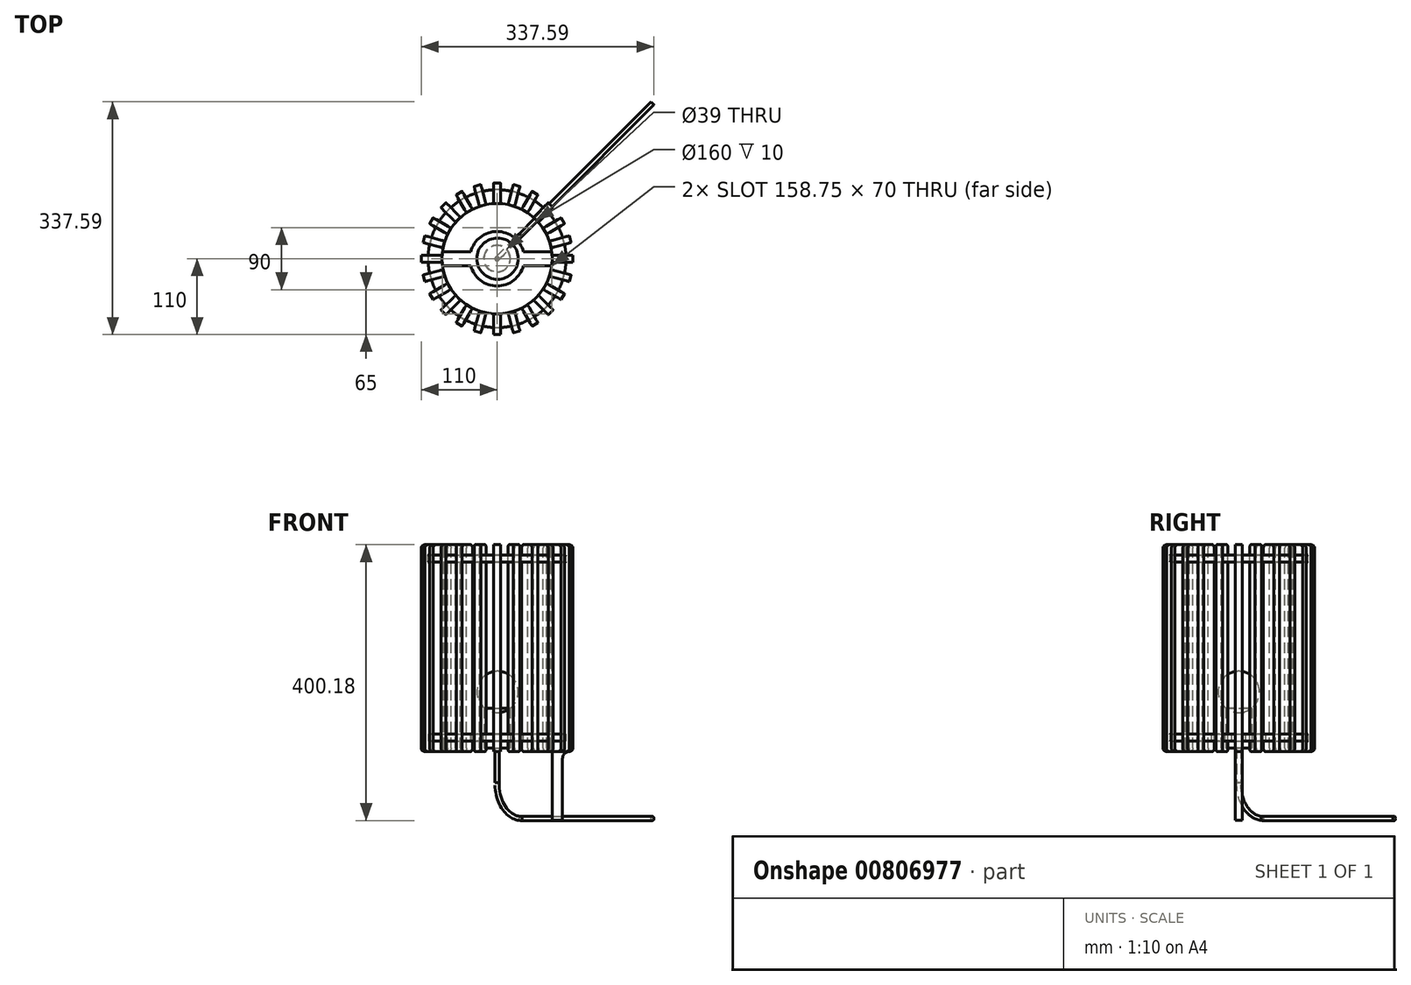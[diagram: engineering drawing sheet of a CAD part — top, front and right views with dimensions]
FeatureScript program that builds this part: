
annotation { "Feature Type Name" : "Feature", "Feature Type Description" : "" }
export const myFeature = defineFeature(function(context is Context, id is Id, definition is map)
    precondition{}
    {
        {
            var Q0;
            Q0=qCreatedBy(makeId("Top.planeOp"),FACE);
            var sketch = newSketch(context, id + "F0", { "sketchPlane" : qUnion([Q0])});
            skCircle(sketch, "E0", {"center": v(0, 0) * mm, "radius": 100 * mm});
            skSolve(sketch);
        }
        {
            var Q0;
            Q0=qSketchRegion(id+"F0",true);
            extrude(context, id + "F1", {"entities" : qUnion([Q0]), "depth" : 10 * mm, "offsetDistance" : 25 * mm});
        }
        {
            var Q0;
            Q0=qCreatedBy(makeId("Front.planeOp"),FACE);
            var sketch = newSketch(context, id + "F2", { "sketchPlane" : qUnion([Q0])});
            skLineSegment(sketch, "E1.bottom", {"start": v(80, -15) * mm, "end": v(110, -15) * mm});
            skLineSegment(sketch, "E1.top", {"start": v(80, 285) * mm, "end": v(110, 285) * mm});
            skLineSegment(sketch, "E1.left", {"start": v(80, -15) * mm, "end": v(80, 285) * mm});
            skLineSegment(sketch, "E1.right", {"start": v(110, -15) * mm, "end": v(110, 285) * mm});
            skSolve(sketch);
        }
        {
            var Q0;
            Q0=qSketchRegion(id+"F2",true);
            extrude(context, id + "F3", {"entities" : qUnion([Q0]), "depth" : 5 * mm, "offsetDistance" : 25 * mm, "hasSecondDirection" : true, "secondDirectionOppositeDirection" : true, "secondDirectionDepth" : 5 * mm});
        }
        {
            var Q0;
            Q0=makeQuery(id+"F3.opExtrude","SWEPT_EDGE",EDGE,{"disambiguationData":[OSD([sQuery(id+"F2.wireOp",EDGE,"E1.top"),sQuery(id+"F2.wireOp",EDGE,"E1.right")])]});
            var Q1;
            Q1=makeQuery(id+"F3.opExtrude","SWEPT_EDGE",EDGE,{"disambiguationData":[OSD([sQuery(id+"F2.wireOp",EDGE,"E1.top"),sQuery(id+"F2.wireOp",EDGE,"E1.left")])]});
            var Q2;
            Q2=makeQuery(id+"F3.opExtrude","SWEPT_EDGE",EDGE,{"disambiguationData":[OSD([sQuery(id+"F2.wireOp",EDGE,"E1.bottom"),sQuery(id+"F2.wireOp",EDGE,"E1.right")])]});
            var Q3;
            Q3=makeQuery(id+"F3.opExtrude","SWEPT_EDGE",EDGE,{"disambiguationData":[OSD([sQuery(id+"F2.wireOp",EDGE,"E1.bottom"),sQuery(id+"F2.wireOp",EDGE,"E1.left")])]});
            fillet(context, id + "F4", {"entities" : qUnion([Q0, Q1, Q2, Q3]), "radius" : 5 * mm, "tangentPropagation" : true, "allowEdgeOverflow" : false});
        }
        {
            var Q0;
            Q0=makeQuery(id+"F3.opExtrude","SWEPT_BODY",BODY,{"disambiguationData":[OSD([sQuery(id+"F2.wireOp",EDGE,"E1.bottom"),sQuery(id+"F2.wireOp",EDGE,"E1.top"),sQuery(id+"F2.wireOp",EDGE,"E1.left"),sQuery(id+"F2.wireOp",EDGE,"E1.right")])]});
            var Q1;
            Q1=makeQuery(id+"F1.opExtrude","SWEPT_FACE",FACE,{"disambiguationData":[OSD([sQuery(id+"F0.wireOp",EDGE,"E0")])]});
            circularPattern(context, id + "F5", {"entities" : qUnion([Q0]), "axis" : qUnion([Q1]), "angle" : 360 * degree, "instanceCount" : 24, "equalSpace" : true});
        }
        {
            var Q0;
            Q0=qCreatedBy(makeId("Top.planeOp"),FACE);
            cPlane(context, id + "F6", {"entities" : qUnion([Q0]), "cplaneType" : CPlaneType.OFFSET, "offset" : 135 * mm, "width" : 150 * mm, "height" : 150 * mm});
        }
        {
            var Q0;
            Q0=makeQuery(id+"F1.opExtrude","CAP_FACE",FACE,{"disambiguationData":[OSD([sQuery(id+"F0.wireOp",EDGE,"E0")])],"isStart":false});
            var sketch = newSketch(context, id + "F7", { "sketchPlane" : qUnion([Q0])});
            skCircle(sketch, "E2", {"center": v(0, 0) * mm, "radius": 80 * mm});
            skSolve(sketch);
        }
        {
            var Q0;
            Q0=qSketchRegion(id+"F7",true);
            extrude(context, id + "F8", {"entities" : qUnion([Q0]), "operationType" : NewBodyOperationType.REMOVE, "endBound" : BoundingType.THROUGH_ALL, "oppositeDirection" : true, "depth" : 25 * mm, "offsetDistance" : 25 * mm});
        }
        {
            var Q0;
            Q0=makeQuery(id+"F1.opExtrude","SWEPT_BODY",BODY,{"disambiguationData":[OSD([sQuery(id+"F0.wireOp",EDGE,"E0")])]});
            var Q1;
            Q1=qCreatedBy(id+"F6.planeOp",FACE);
            mirror(context, id + "F9", {"entities" : qUnion([Q0]), "mirrorPlane" : qUnion([Q1])});
        }
        {
            var Q0;
            Q0=qCreatedBy(makeId("Front.planeOp"),FACE);
            var sketch = newSketch(context, id + "F10", { "sketchPlane" : qUnion([Q0])});
            skLineSegment(sketch, "E3.1", {"start": v(80, 285) * mm, "end": v(110, 285) * mm, "construction": true});
            skLineSegment(sketch, "E3.2", {"start": v(80, -15) * mm, "end": v(80, 285) * mm, "construction": true});
            skLineSegment(sketch, "E3.3", {"start": v(110, -8.74) * mm, "end": v(110, 285) * mm, "construction": true});
            skPoint(sketch, "E3.0.end.orphan", {"position": v(110, -15) * mm});
            skPoint(sketch, "E3.0.start.orphan", {"position": v(80, -15) * mm});
            skLineSegment(sketch, "E4.top", {"start": v(80, -8.74) * mm, "end": v(110, -8.74) * mm});
            skLineSegment(sketch, "E4.left", {"start": v(80, -15) * mm, "end": v(80, -8.74) * mm});
            skLineSegment(sketch, "E5", {"start": v(80, -15) * mm, "end": v(80, -115) * mm});
            skLineSegment(sketch, "E6", {"start": v(80, -115) * mm, "end": v(95, -115) * mm});
            skLineSegment(sketch, "E7", {"start": v(95, -115) * mm, "end": v(95, -25) * mm});
            skPoint(sketch, "E8.visualSharp", {"position": v(95, -15) * mm});
            skArc(sketch, "E8.filletArc", {"start": v(105, -15) * mm, "mid": v(97.93, -17.93) * mm, "end": v(95, -25) * mm});
            skPoint(sketch, "E9.right.end.orphan", {"position": v(110, -135) * mm});
            skLineSegment(sketch, "E10", {"start": v(105, -15) * mm, "end": v(110, -8.74) * mm});
            skSolve(sketch);
        }
        {
            var Q0;
            Q0=qSketchRegion(id+"F10",true);
            extrude(context, id + "F11", {"entities" : qUnion([Q0]), "operationType" : NewBodyOperationType.ADD, "depth" : 5 * mm, "offsetDistance" : 25 * mm, "hasSecondDirection" : true, "secondDirectionOppositeDirection" : true, "secondDirectionDepth" : 5 * mm});
        }
        {
            var Q0;
            Q0=makeQuery(id+"F1.opExtrude","CAP_FACE",FACE,{"disambiguationData":[OSD([sQuery(id+"F0.wireOp",EDGE,"E0")])],"isStart":false});
            var sketch = newSketch(context, id + "F12", { "sketchPlane" : qUnion([Q0])});
            skLineSegment(sketch, "E11.bottom", {"start": v(-83.67, -10) * mm, "end": v(-38.21, -10) * mm});
            skLineSegment(sketch, "E11.top", {"start": v(-83.67, 10) * mm, "end": v(-38.21, 10) * mm});
            skLineSegment(sketch, "E11.left", {"start": v(-83.67, -10) * mm, "end": v(-83.67, 10) * mm});
            skLineSegment(sketch, "E11.right", {"start": v(83.67, -10) * mm, "end": v(83.67, 10) * mm});
            skPoint(sketch, "E11.middle", {"position": v(0, 0) * mm});
            skCircle(sketch, "E12", {"center": v(0, 0) * mm, "radius": 19.5 * mm});
            skArc(sketch, "E13", {"start": v(-38.21, -10) * mm, "mid": v(0, -39.5) * mm, "end": v(38.21, -10) * mm});
            skLineSegment(sketch, "E14.trimOffspring", {"start": v(38.21, -10) * mm, "end": v(83.67, -10) * mm});
            skLineSegment(sketch, "E15.trimOffspring", {"start": v(38.21, 10) * mm, "end": v(83.67, 10) * mm});
            skArc(sketch, "E16.trimOffspring", {"start": v(38.21, 10) * mm, "mid": v(0, 39.5) * mm, "end": v(-38.21, 10) * mm});
            skSolve(sketch);
        }
        {
            var Q0;
            Q0=qSketchRegion(id+"F12",true);
            extrude(context, id + "F13", {"entities" : qUnion([Q0]), "operationType" : NewBodyOperationType.ADD, "oppositeDirection" : true, "depth" : 10 * mm, "offsetDistance" : 25 * mm});
        }
        {
            var Q0;
            Q0=makeQuery(id+"F13.boolean.opBoolean","MERGE",FACE,{"derivedFrom":[makeQuery(id+"F1.opExtrude","CAP_FACE",FACE,{"disambiguationData":[OSD([sQuery(id+"F0.wireOp",EDGE,"E0")])],"isStart":false}),makeQuery(id+"F13.opExtrude","CAP_FACE",FACE,{"disambiguationData":[OSD([sQuery(id+"F12.wireOp",EDGE,"E11.bottom"),sQuery(id+"F12.wireOp",EDGE,"E11.top"),sQuery(id+"F12.wireOp",EDGE,"E11.left"),sQuery(id+"F12.wireOp",EDGE,"E11.right"),sQuery(id+"F12.wireOp",EDGE,"E12"),sQuery(id+"F12.wireOp",EDGE,"E13"),sQuery(id+"F12.wireOp",EDGE,"E14.trimOffspring"),sQuery(id+"F12.wireOp",EDGE,"E15.trimOffspring"),sQuery(id+"F12.wireOp",EDGE,"E16.trimOffspring")])],"isStart":true})]});
            var sketch = newSketch(context, id + "F14", { "sketchPlane" : qUnion([Q0])});
            skCircle(sketch, "E17", {"center": v(0, 0) * mm, "radius": 19 * mm});
            skSolve(sketch);
        }
        {
            var Q0;
            Q0=qSketchRegion(id+"F14",true);
            extrude(context, id + "F15", {"entities" : qUnion([Q0]), "depth" : 38 * mm, "offsetDistance" : 25 * mm, "hasSecondDirection" : true, "secondDirectionOppositeDirection" : true, "secondDirectionDepth" : 20 * mm});
        }
        {
            var Q0;
            Q0=qCreatedBy(makeId("Front.planeOp"),FACE);
            var sketch = newSketch(context, id + "F16", { "sketchPlane" : qUnion([Q0])});
            skArc(sketch, "E18", {"start": v(0.71, 101.44) * mm, "mid": v(-29.29, 71.44) * mm, "end": v(0.71, 41.44) * mm});
            skLineSegment(sketch, "E19", {"start": v(0.71, 101.44) * mm, "end": v(0.71, 41.44) * mm});
            skSolve(sketch);
        }
        {
            var Q0;
            Q0=qSketchRegion(id+"F16",true);
            var Q1;
            Q1=sQuery(id+"F16.wireOp",EDGE,"E19");
            revolve(context, id + "F17", {"surfaceOperationType" : NewSurfaceOperationType.NEW, "entities" : qUnion([Q0]), "axis" : qUnion([Q1]), "revolveType" : RevolveType.FULL});
        }
        {
            var Q0;
            Q0=qCreatedBy(makeId("Front.planeOp"),FACE);
            var Q1;
            Q1=qCreatedBy(makeId("Right.planeOp"),FACE);
            cPlane(context, id + "F18", {"entities" : qUnion([Q0, Q1]), "cplaneType" : CPlaneType.MID_PLANE, "offset" : 25 * mm, "flipAlignment" : true, "width" : 150 * mm, "height" : 150 * mm});
        }
        {
            var Q0;
            Q0=qCreatedBy(id+"F18.planeOp",FACE);
            var sketch = newSketch(context, id + "F19", { "sketchPlane" : qUnion([Q0])});
            skLineSegment(sketch, "E20", {"start": v(0.18, -11.7) * mm, "end": v(0.18, -62) * mm});
            skLineSegment(sketch, "E21", {"start": v(50.18, -112) * mm, "end": v(320.55, -112) * mm});
            skPoint(sketch, "E22.visualSharp", {"position": v(0.18, -112) * mm});
            skArc(sketch, "E22.filletArc", {"start": v(0.18, -62) * mm, "mid": v(14.82, -97.36) * mm, "end": v(50.18, -112) * mm});
            skSolve(sketch);
        }
        {
            var Q0;
            Q0=makeQuery(id+"F15.opExtrude","CAP_FACE",FACE,{"disambiguationData":[OSD([sQuery(id+"F14.wireOp",EDGE,"E17")])],"isStart":true});
            var sketch = newSketch(context, id + "F20", { "sketchPlane" : qUnion([Q0])});
            skCircle(sketch, "E23", {"center": v(0, 0) * mm, "radius": 3 * mm});
            skSolve(sketch);
        }
        {
            var Q0;
            Q0=qSketchRegion(id+"F20",true);
            var Q1;
            Q1=qConstructionFilter(qBodyType(qCreatedBy(id+"F19",EDGE),BodyType.WIRE),ConstructionObject.NO);
            sweep(context, id + "F21", {"profiles" : qUnion([Q0]), "path" : qUnion([Q1])});
        }
    });
